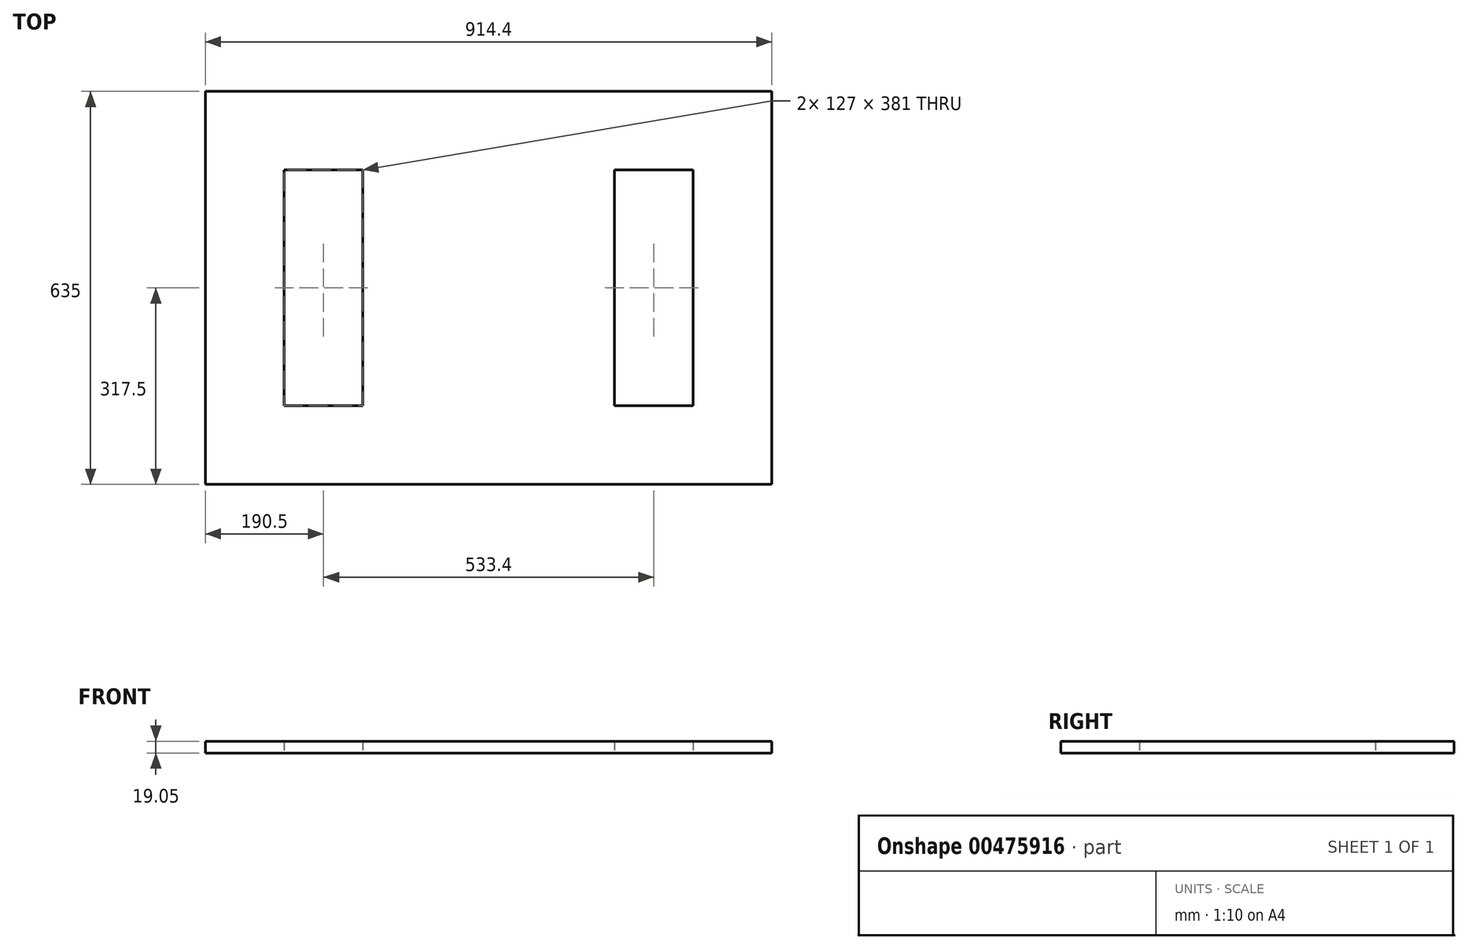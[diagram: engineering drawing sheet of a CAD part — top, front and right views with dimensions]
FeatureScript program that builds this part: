
annotation { "Feature Type Name" : "Feature", "Feature Type Description" : "" }
export const myFeature = defineFeature(function(context is Context, id is Id, definition is map)
    precondition{}
    {
        {
            var Q0;
            Q0=qCreatedBy(makeId("Top.planeOp"),FACE);
            var sketch = newSketch(context, id + "F0", { "sketchPlane" : qUnion([Q0])});
            skLineSegment(sketch, "E0.bottom", {"start": v(457.2, 317.5) * mm, "end": v(-457.2, 317.5) * mm});
            skLineSegment(sketch, "E0.top", {"start": v(457.2, -317.5) * mm, "end": v(-457.2, -317.5) * mm});
            skLineSegment(sketch, "E0.left", {"start": v(457.2, 317.5) * mm, "end": v(457.2, -317.5) * mm});
            skLineSegment(sketch, "E0.right", {"start": v(-457.2, 317.5) * mm, "end": v(-457.2, -317.5) * mm});
            skPoint(sketch, "E0.middle", {"position": v(0, 0) * mm});
            skSolve(sketch);
        }
        {
            var Q0;
            Q0 = qSketchRegion(id + "F0", true);
            extrude(context, id + "F1", {"entities" : qUnion([Q0]), "endBound" : BoundingType.SYMMETRIC, "depth" : 12.7 * mm, "offsetDistance" : 25.4 * mm});
        }
        {
            var Q0;
            Q0 = qSketchRegion(id + "F0", true);
            extrude(context, id + "F2", {"entities" : qUnion([Q0]), "operationType" : NewBodyOperationType.ADD, "depth" : 12.7 * mm, "offsetDistance" : 25.4 * mm});
        }
        {
            var Q0;
            Q0=makeQuery(id+"F1.opExtrude","CAP_FACE",FACE,{"disambiguationData":[OSD([sQuery(id+"F0.wireOp",EDGE,"E0.bottom"),sQuery(id+"F0.wireOp",EDGE,"E0.top"),sQuery(id+"F0.wireOp",EDGE,"E0.left"),sQuery(id+"F0.wireOp",EDGE,"E0.right")])],"isStart":true});
            var sketch = newSketch(context, id + "F3", { "sketchPlane" : qUnion([Q0])});
            skLineSegment(sketch, "E1.bottom", {"start": v(-330.2, -190.5) * mm, "end": v(-203.2, -190.5) * mm});
            skLineSegment(sketch, "E1.top", {"start": v(-330.2, 190.5) * mm, "end": v(-203.2, 190.5) * mm});
            skLineSegment(sketch, "E1.left", {"start": v(-330.2, -190.5) * mm, "end": v(-330.2, 190.5) * mm});
            skLineSegment(sketch, "E1.right", {"start": v(-203.2, -190.5) * mm, "end": v(-203.2, 190.5) * mm});
            skLineSegment(sketch, "E2.bottom", {"start": v(203.2, -190.5) * mm, "end": v(330.2, -190.5) * mm});
            skLineSegment(sketch, "E2.top", {"start": v(203.2, 190.5) * mm, "end": v(330.2, 190.5) * mm});
            skLineSegment(sketch, "E2.left", {"start": v(203.2, -190.5) * mm, "end": v(203.2, 190.5) * mm});
            skLineSegment(sketch, "E2.right", {"start": v(330.2, -190.5) * mm, "end": v(330.2, 190.5) * mm});
            skSolve(sketch);
        }
        {
            var Q0;
            Q0 = qSketchRegion(id + "F3", true);
            extrude(context, id + "F4", {"entities" : qUnion([Q0]), "operationType" : NewBodyOperationType.REMOVE, "oppositeDirection" : true, "depth" : 73.66 * mm, "offsetDistance" : 25.4 * mm});
        }
    });
